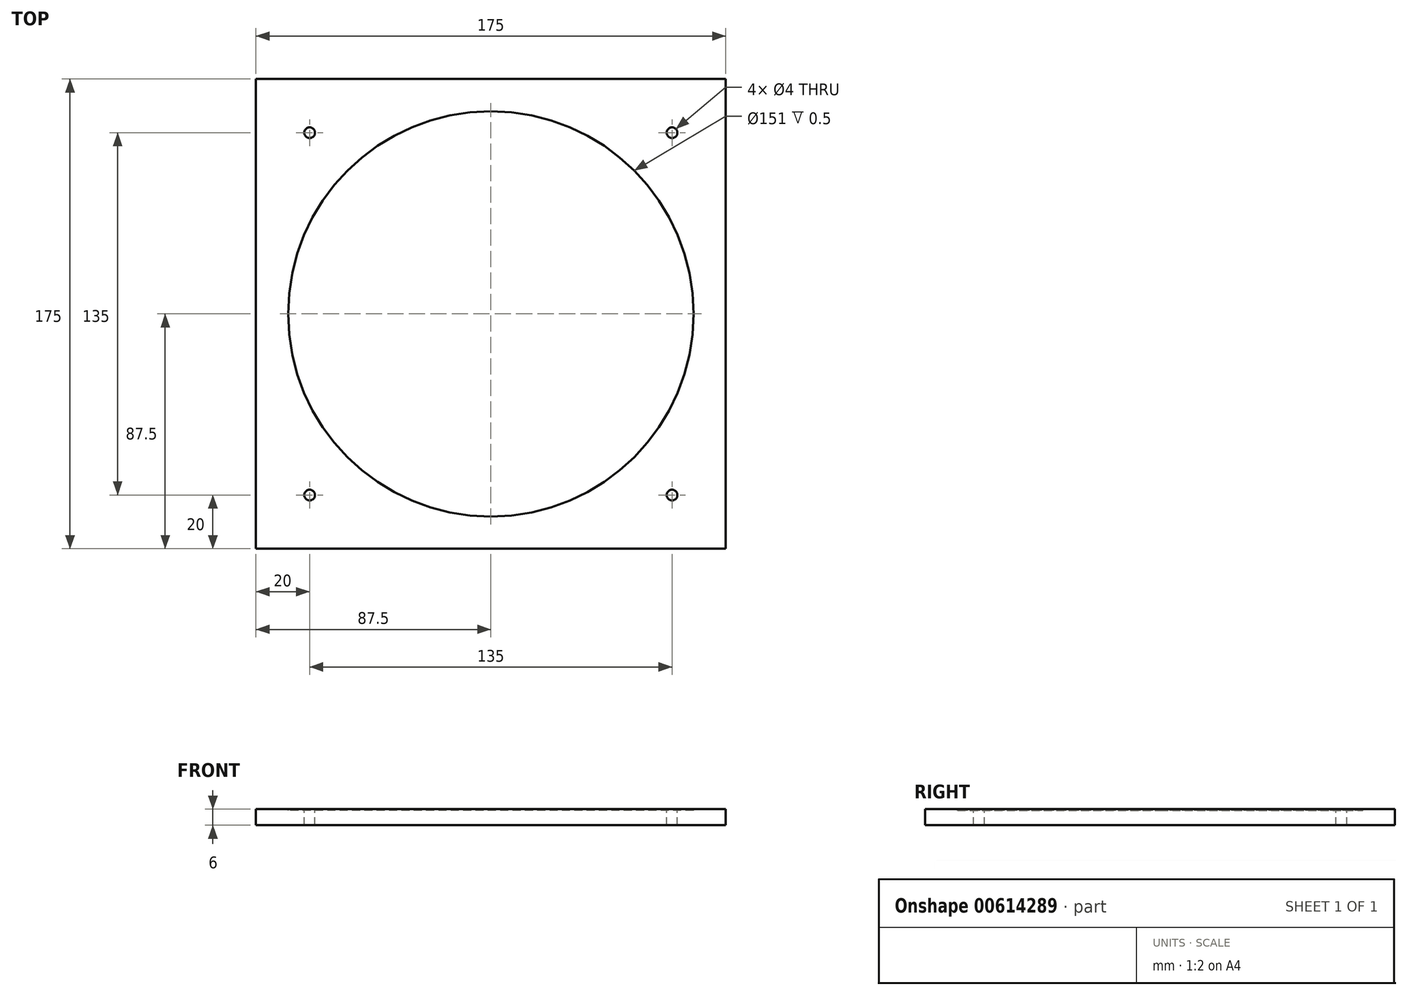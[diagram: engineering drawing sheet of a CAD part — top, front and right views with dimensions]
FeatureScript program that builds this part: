
annotation { "Feature Type Name" : "Feature", "Feature Type Description" : "" }
export const myFeature = defineFeature(function(context is Context, id is Id, definition is map)
    precondition{}
    {
        {
            var Q0;
            Q0=qCreatedBy(makeId("Top.planeOp"),FACE);
            var sketch = newSketch(context, id + "F0", { "sketchPlane" : qUnion([Q0])});
            skLineSegment(sketch, "E0.bottom", {"start": v(0, 0) * mm, "end": v(175, 0) * mm});
            skLineSegment(sketch, "E0.top", {"start": v(0, 175) * mm, "end": v(175, 175) * mm});
            skLineSegment(sketch, "E0.left", {"start": v(0, 0) * mm, "end": v(0, 175) * mm});
            skLineSegment(sketch, "E0.right", {"start": v(175, 0) * mm, "end": v(175, 175) * mm});
            skSolve(sketch);
        }
        {
            var Q0;
            Q0=makeQuery(id+"F0.imprint","IMPRINT",FACE,{"disambiguationData":[TD([[makeQuery(id+"F0.imprint","IMPRINT",EDGE,{"derivedFrom":sQuery(id+"F0.wireOp",EDGE,"E0.bottom")}),1.0]])]});
            extrude(context, id + "F1", {"entities" : qUnion([Q0]), "depth" : 6 * mm, "offsetDistance" : 25 * mm});
        }
        {
            var Q0;
            Q0=makeQuery(id+"F1.opExtrude","CAP_FACE",FACE,{"disambiguationData":[OSD([sQuery(id+"F0.wireOp",EDGE,"E0.bottom"),sQuery(id+"F0.wireOp",EDGE,"E0.top"),sQuery(id+"F0.wireOp",EDGE,"E0.left"),sQuery(id+"F0.wireOp",EDGE,"E0.right")])],"isStart":false});
            var sketch = newSketch(context, id + "F2", { "sketchPlane" : qUnion([Q0])});
            skCircle(sketch, "E1", {"center": v(87.5, 87.5) * mm, "radius": 75.5 * mm});
            skSolve(sketch);
        }
        {
            var Q0;
            Q0=makeQuery(id+"F2.imprint","IMPRINT",FACE,{"disambiguationData":[TD([[makeQuery(id+"F2.imprint","IMPRINT",EDGE,{"derivedFrom":sQuery(id+"F2.wireOp",EDGE,"E1")}),1.0]])]});
            extrude(context, id + "F3", {"entities" : qUnion([Q0]), "operationType" : NewBodyOperationType.REMOVE, "oppositeDirection" : true, "depth" : .5 * mm, "offsetDistance" : 25 * mm});
        }
        {
            var Q0;
            Q0=makeQuery(id+"F1.opExtrude","CAP_FACE",FACE,{"disambiguationData":[OSD([sQuery(id+"F0.wireOp",EDGE,"E0.bottom"),sQuery(id+"F0.wireOp",EDGE,"E0.top"),sQuery(id+"F0.wireOp",EDGE,"E0.left"),sQuery(id+"F0.wireOp",EDGE,"E0.right")])],"isStart":false});
            var sketch = newSketch(context, id + "F4", { "sketchPlane" : qUnion([Q0])});
            skCircle(sketch, "E2", {"center": v(20, 155) * mm, "radius": 2 * mm});
            skCircle(sketch, "E3", {"center": v(155, 155) * mm, "radius": 2 * mm});
            skCircle(sketch, "E4", {"center": v(20, 20) * mm, "radius": 2 * mm});
            skCircle(sketch, "E5", {"center": v(155, 20) * mm, "radius": 2 * mm});
            skSolve(sketch);
        }
        {
            var Q0;
            Q0=makeQuery(id+"F4.imprint","IMPRINT",FACE,{"disambiguationData":[TD([[makeQuery(id+"F4.imprint","IMPRINT",EDGE,{"derivedFrom":sQuery(id+"F4.wireOp",EDGE,"E2")}),1.0]])]});
            var Q1;
            Q1=makeQuery(id+"F4.imprint","IMPRINT",FACE,{"disambiguationData":[TD([[makeQuery(id+"F4.imprint","IMPRINT",EDGE,{"derivedFrom":sQuery(id+"F4.wireOp",EDGE,"E3")}),1.0]])]});
            var Q2;
            Q2=makeQuery(id+"F4.imprint","IMPRINT",FACE,{"disambiguationData":[TD([[makeQuery(id+"F4.imprint","IMPRINT",EDGE,{"derivedFrom":sQuery(id+"F4.wireOp",EDGE,"E5")}),1.0]])]});
            var Q3;
            Q3=makeQuery(id+"F4.imprint","IMPRINT",FACE,{"disambiguationData":[TD([[makeQuery(id+"F4.imprint","IMPRINT",EDGE,{"derivedFrom":sQuery(id+"F4.wireOp",EDGE,"E4")}),1.0]])]});
            extrude(context, id + "F5", {"entities" : qUnion([Q0, Q1, Q2, Q3]), "operationType" : NewBodyOperationType.REMOVE, "endBound" : BoundingType.THROUGH_ALL, "oppositeDirection" : true, "depth" : 25 * mm, "offsetDistance" : 25 * mm});
        }
    });
